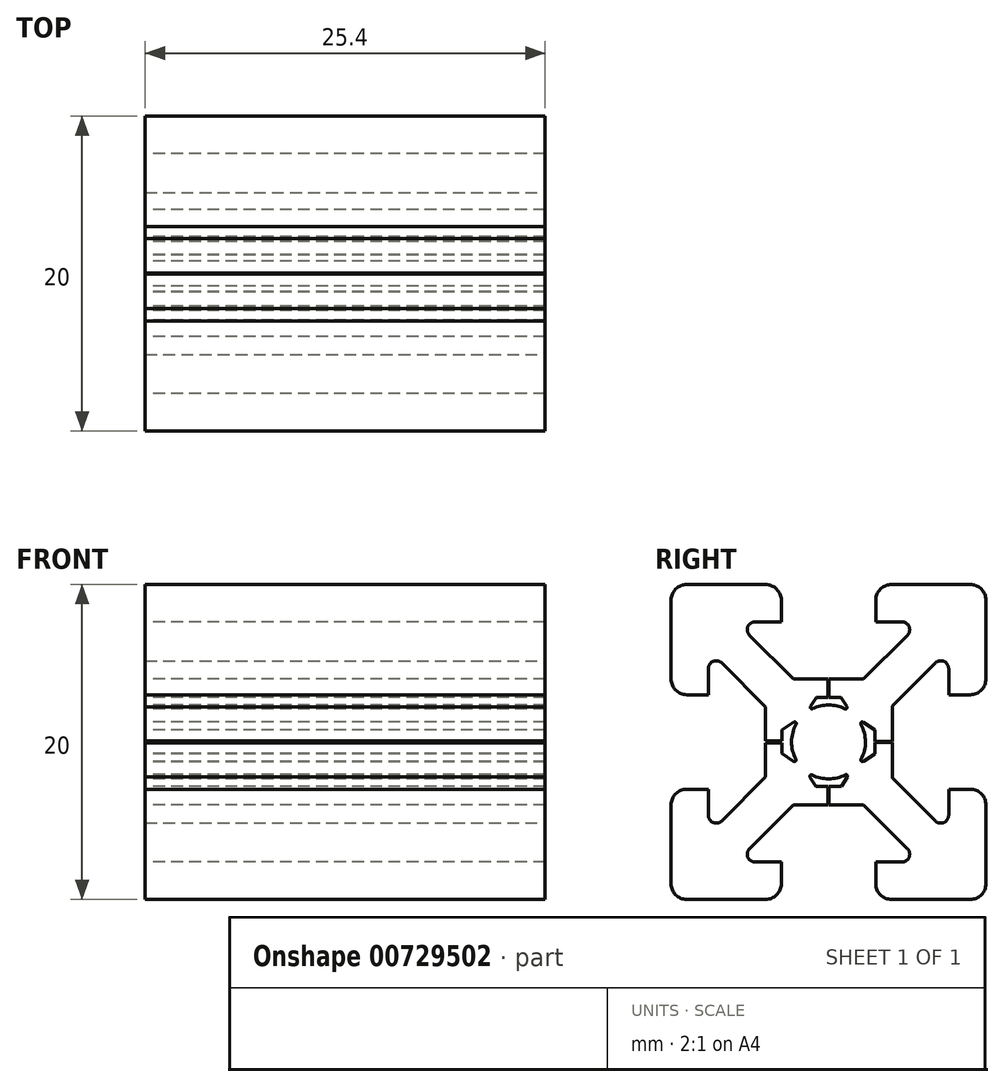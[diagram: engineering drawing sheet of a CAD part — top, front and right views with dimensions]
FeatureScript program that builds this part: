
annotation { "Feature Type Name" : "Feature", "Feature Type Description" : "" }
export const myFeature = defineFeature(function(context is Context, id is Id, definition is map)
    precondition{}
    {
        {
            var Q0;
            Q0=qCreatedBy(makeId("Top.planeOp"),FACE);
            var sketch = newSketch(context, id + "F0", { "sketchPlane" : qUnion([Q0])});
            skLineSegment(sketch, "E0", {"start": v(-15.81, 0) * mm, "end": v(2.4, 0) * mm, "construction": true});
            skLineSegment(sketch, "E1", {"start": v(0, 15.89) * mm, "end": v(0, -13.7) * mm, "construction": true});
            skLineSegment(sketch, "E2", {"start": v(0, 0) * mm, "end": v(-1.66, 1.66) * mm, "construction": true});
            skLineSegment(sketch, "E3", {"start": v(-2.3, 4.06) * mm, "end": v(-5.86, 7.63) * mm});
            skLineSegment(sketch, "E4", {"start": v(-5.86, 7.63) * mm, "end": v(-3, 7.63) * mm});
            skLineSegment(sketch, "E5", {"start": v(-3, 7.63) * mm, "end": v(-3, 10) * mm});
            skLineSegment(sketch, "E6", {"start": v(-3, 10) * mm, "end": v(-10, 10) * mm});
            skLineSegment(sketch, "E7.MirrorCS", {"start": v(-4, 2.23) * mm, "end": v(-7.63, 5.86) * mm});
            skLineSegment(sketch, "E8.MirrorCS", {"start": v(-7.63, 3) * mm, "end": v(-10, 3) * mm});
            skLineSegment(sketch, "E9.MirrorCS", {"start": v(-10, 3) * mm, "end": v(-10, 10) * mm});
            skLineSegment(sketch, "E10.MirrorCS", {"start": v(-7.63, 5.86) * mm, "end": v(-7.63, 3) * mm});
            skLineSegment(sketch, "E11.MirrorCS", {"start": v(3, 10) * mm, "end": v(10, 10) * mm});
            skLineSegment(sketch, "E12.MirrorCS", {"start": v(5.86, 7.63) * mm, "end": v(3, 7.63) * mm});
            skLineSegment(sketch, "E13.MirrorCS", {"start": v(3, 7.63) * mm, "end": v(3, 10) * mm});
            skLineSegment(sketch, "E14.MirrorCS", {"start": v(7.63, 5.86) * mm, "end": v(7.63, 3) * mm});
            skLineSegment(sketch, "E15.MirrorCS", {"start": v(10, 3) * mm, "end": v(10, 10) * mm});
            skLineSegment(sketch, "E16.MirrorCS", {"start": v(7.63, 3) * mm, "end": v(10, 3) * mm});
            skLineSegment(sketch, "E17.MirrorCS", {"start": v(2.3, 4.06) * mm, "end": v(5.86, 7.63) * mm});
            skLineSegment(sketch, "E18.MirrorCS", {"start": v(4, 2.23) * mm, "end": v(7.63, 5.86) * mm});
            skLineSegment(sketch, "E19.MirrorCS", {"start": v(5.86, -7.63) * mm, "end": v(3, -7.63) * mm});
            skLineSegment(sketch, "E20.MirrorCS", {"start": v(3, -10) * mm, "end": v(10, -10) * mm});
            skLineSegment(sketch, "E21.MirrorCS", {"start": v(-5.86, -7.63) * mm, "end": v(-3, -7.63) * mm});
            skLineSegment(sketch, "E22.MirrorCS", {"start": v(-3, -10) * mm, "end": v(-10, -10) * mm});
            skLineSegment(sketch, "E23.MirrorCS", {"start": v(-3, -7.63) * mm, "end": v(-3, -10) * mm});
            skLineSegment(sketch, "E24.MirrorCS", {"start": v(3, -7.63) * mm, "end": v(3, -10) * mm});
            skLineSegment(sketch, "E25.MirrorCS", {"start": v(7.63, -5.86) * mm, "end": v(7.63, -3) * mm});
            skLineSegment(sketch, "E26.MirrorCS", {"start": v(10, -3) * mm, "end": v(10, -10) * mm});
            skLineSegment(sketch, "E27.MirrorCS", {"start": v(4, -2.23) * mm, "end": v(7.63, -5.86) * mm});
            skLineSegment(sketch, "E28.MirrorCS", {"start": v(-7.63, -5.86) * mm, "end": v(-7.63, -3) * mm});
            skLineSegment(sketch, "E29.MirrorCS", {"start": v(-10, -3) * mm, "end": v(-10, -10) * mm});
            skLineSegment(sketch, "E30.MirrorCS", {"start": v(-7.63, -3) * mm, "end": v(-10, -3) * mm});
            skLineSegment(sketch, "E31.MirrorCS", {"start": v(-4, -2.23) * mm, "end": v(-7.63, -5.86) * mm});
            skLineSegment(sketch, "E32.MirrorCS", {"start": v(2.23, -4) * mm, "end": v(5.86, -7.63) * mm});
            skLineSegment(sketch, "E33.MirrorCS", {"start": v(-2.23, -4) * mm, "end": v(-5.86, -7.63) * mm});
            skLineSegment(sketch, "E34.MirrorCS", {"start": v(7.63, -3) * mm, "end": v(10, -3) * mm});
            skLineSegment(sketch, "E35", {"start": v(-4, 0) * mm, "end": v(-4, 0) * mm});
            skLineSegment(sketch, "E36", {"start": v(-2.3, 4.06) * mm, "end": v(-0.02, 4.06) * mm});
            skLineSegment(sketch, "E37.MirrorCS", {"start": v(-15.81, 8.12) * mm, "end": v(21.32, 8.12) * mm, "construction": true});
            skLineSegment(sketch, "E38", {"start": v(-4, 2.23) * mm, "end": v(-4, 0.02) * mm});
            skLineSegment(sketch, "E39", {"start": v(-2.23, -4) * mm, "end": v(-0.05, -4) * mm});
            skLineSegment(sketch, "E40", {"start": v(4, 2.23) * mm, "end": v(4, 0.03) * mm});
            skPoint(sketch, "E41.orphan", {"position": v(-0.59, 2.36) * mm});
            skPoint(sketch, "E42.orphan", {"position": v(-2.36, 0.59) * mm});
            skLineSegment(sketch, "E43.trimOffspring", {"start": v(0.03, 4.06) * mm, "end": v(2.3, 4.06) * mm});
            skPoint(sketch, "E44.orphan", {"position": v(0.59, 2.36) * mm});
            skPoint(sketch, "E45.orphan", {"position": v(2.36, 0.59) * mm});
            skPoint(sketch, "E46.orphan", {"position": v(-2.36, -0.59) * mm});
            skPoint(sketch, "E47.orphan", {"position": v(-0.59, -2.36) * mm});
            skPoint(sketch, "E48.orphan", {"position": v(0.59, -2.36) * mm});
            skPoint(sketch, "E49.orphan", {"position": v(2.36, -0.59) * mm});
            skLineSegment(sketch, "E50", {"start": v(-2.4, 0.03) * mm, "end": v(-2.4, 0.03) * mm});
            skLineSegment(sketch, "E51.MirrorCS", {"start": v(-2.4, -0.03) * mm, "end": v(-2.4, -0.03) * mm});
            skLineSegment(sketch, "E52.MirrorCS", {"start": v(2.4, 0.03) * mm, "end": v(2.4, 0.03) * mm});
            skLineSegment(sketch, "E53.MirrorCS", {"start": v(2.4, -0.03) * mm, "end": v(2.4, -0.03) * mm});
            skLineSegment(sketch, "E54.trimOffspring", {"start": v(4, -0.03) * mm, "end": v(4, -2.23) * mm});
            skLineSegment(sketch, "E55.trimOffspring", {"start": v(-4, -0.03) * mm, "end": v(-4, -2.23) * mm});
            skPoint(sketch, "E56.end.orphan", {"position": v(-2.4, 0) * mm});
            skPoint(sketch, "E57.orphan", {"position": v(-4, 0.03) * mm});
            skPoint(sketch, "E58.MirrorCS.end.orphan", {"position": v(2.4, 0) * mm});
            skPoint(sketch, "E58.MirrorCS.start.orphan", {"position": v(2.4, -0.03) * mm});
            skPoint(sketch, "E59.MirrorCS.start.orphan", {"position": v(2.4, 0.03) * mm});
            skLineSegment(sketch, "E60.trimOffspring", {"start": v(0.05, -4) * mm, "end": v(2.23, -4) * mm});
            skLineSegment(sketch, "E61", {"start": v(0, 0) * mm, "end": v(10, 10) * mm, "construction": true});
            skLineSegment(sketch, "E62", {"start": v(0, 0) * mm, "end": v(-10, -10) * mm, "construction": true});
            skLineSegment(sketch, "E63", {"start": v(10, -10) * mm, "end": v(0.07, 0.07) * mm, "construction": true});
            skPoint(sketch, "E64.start.orphan", {"position": v(-4, -0.03) * mm});
            skLineSegment(sketch, "E65", {"start": v(-2.82, -0.78) * mm, "end": v(-1.9, -1.37) * mm});
            skPoint(sketch, "E66.orphan", {"position": v(-1.66, -1.66) * mm});
            skPoint(sketch, "E67.orphan", {"position": v(0.03, -4.06) * mm});
            skPoint(sketch, "E68.orphan", {"position": v(-0.03, -4.06) * mm});
            skLineSegment(sketch, "E69", {"start": v(-2.82, 0.8) * mm, "end": v(-1.87, 1.41) * mm});
            skLineSegment(sketch, "E70", {"start": v(-0.76, 2.95) * mm, "end": v(-1.54, 1.77) * mm});
            skLineSegment(sketch, "E71", {"start": v(0.76, 2.95) * mm, "end": v(1.51, 1.8) * mm});
            skLineSegment(sketch, "E72", {"start": v(2.82, 0.8) * mm, "end": v(1.83, 1.46) * mm});
            skLineSegment(sketch, "E73", {"start": v(2.82, -0.8) * mm, "end": v(1.87, -1.41) * mm});
            skLineSegment(sketch, "E74.trimOffspring", {"start": v(1.8, -1.68) * mm, "end": v(1.82, -1.66) * mm});
            skLineSegment(sketch, "E75.trimOffspring", {"start": v(-8.12, 8.12) * mm, "end": v(-29.35, 29.35) * mm, "construction": true});
            skLineSegment(sketch, "E76", {"start": v(0.74, -2.96) * mm, "end": v(1.51, -1.8) * mm});
            skPoint(sketch, "E77.trimOffspring.start.orphan", {"position": v(0.33, -2.4) * mm});
            skPoint(sketch, "E78.MirrorCS.end.orphan", {"position": v(-0.33, -2.4) * mm});
            skLineSegment(sketch, "E79.trimOffspring", {"start": v(2.43, 0) * mm, "end": v(21.32, 0) * mm, "construction": true});
            skPoint(sketch, "E80.trimOffspring.start.orphan", {"position": v(0.33, 2.4) * mm});
            skPoint(sketch, "E81.trimOffspring.start.orphan", {"position": v(-0.33, 2.4) * mm});
            skArc(sketch, "E82", {"start": v(-1.87, 1.41) * mm, "mid": v(-2.35, 0.03) * mm, "end": v(-1.9, -1.37) * mm});
            skArc(sketch, "E83.trimOffspring", {"start": v(1.51, 1.8) * mm, "mid": v(-0.02, 2.35) * mm, "end": v(-1.54, 1.77) * mm});
            skArc(sketch, "E84.trimOffspring", {"start": v(1.87, -1.41) * mm, "mid": v(2.35, 0.03) * mm, "end": v(1.83, 1.46) * mm});
            skArc(sketch, "E85.trimOffspring", {"start": v(-1.55, -1.76) * mm, "mid": v(-0.03, -2.35) * mm, "end": v(1.51, -1.8) * mm});
            skLineSegment(sketch, "E86", {"start": v(-1.55, -1.76) * mm, "end": v(-0.75, -2.96) * mm});
            skLineSegment(sketch, "E87", {"start": v(-4, 0.03) * mm, "end": v(-2.82, 0.03) * mm});
            skLineSegment(sketch, "E88", {"start": v(-2.82, 0.03) * mm, "end": v(-2.82, 0.8) * mm});
            skLineSegment(sketch, "E89", {"start": v(-4, -0.03) * mm, "end": v(-2.82, -0.03) * mm});
            skLineSegment(sketch, "E90", {"start": v(-2.82, -0.03) * mm, "end": v(-2.82, -0.78) * mm});
            skLineSegment(sketch, "E91.MirrorCS", {"start": v(4, 0.03) * mm, "end": v(2.82, 0.03) * mm});
            skLineSegment(sketch, "E92.MirrorCS", {"start": v(4, -0.03) * mm, "end": v(2.82, -0.03) * mm});
            skLineSegment(sketch, "E93", {"start": v(2.82, 0.03) * mm, "end": v(2.82, 0.8) * mm});
            skLineSegment(sketch, "E94", {"start": v(2.82, -0.03) * mm, "end": v(2.82, -0.8) * mm});
            skLineSegment(sketch, "E95", {"start": v(-0.05, -4) * mm, "end": v(-0.05, -2.96) * mm});
            skLineSegment(sketch, "E96", {"start": v(-0.05, -2.96) * mm, "end": v(-0.75, -2.96) * mm});
            skLineSegment(sketch, "E97", {"start": v(0.05, -4) * mm, "end": v(0.05, -2.96) * mm});
            skLineSegment(sketch, "E98", {"start": v(0.05, -2.96) * mm, "end": v(0.74, -2.96) * mm});
            skLineSegment(sketch, "E99", {"start": v(-0.02, 4.06) * mm, "end": v(-0.02, 2.95) * mm});
            skLineSegment(sketch, "E100", {"start": v(-0.02, 2.95) * mm, "end": v(-0.76, 2.95) * mm});
            skLineSegment(sketch, "E101", {"start": v(0.03, 4.06) * mm, "end": v(0.03, 2.95) * mm});
            skLineSegment(sketch, "E102", {"start": v(0.03, 2.95) * mm, "end": v(0.76, 2.95) * mm});
            skSolve(sketch);
        }
        {
            var Q0;
            Q0=qSketchRegion(id+"F0",true);
            extrude(context, id + "F1", {"entities" : qUnion([Q0]), "depth" : 25.4 * mm, "offsetDistance" : 25.4 * mm});
        }
        {
            var Q0;
            Q0=makeQuery(id+"F1.opExtrude","SWEPT_EDGE",EDGE,{"disambiguationData":[OSD([sQuery(id+"F0.wireOp",EDGE,"E15.MirrorCS"),sQuery(id+"F0.wireOp",EDGE,"E11.MirrorCS")])]});
            var Q1;
            Q1=makeQuery(id+"F1.opExtrude","SWEPT_EDGE",EDGE,{"disambiguationData":[OSD([sQuery(id+"F0.wireOp",EDGE,"E20.MirrorCS"),sQuery(id+"F0.wireOp",EDGE,"E26.MirrorCS")])]});
            var Q2;
            Q2=makeQuery(id+"F1.opExtrude","SWEPT_EDGE",EDGE,{"disambiguationData":[OSD([sQuery(id+"F0.wireOp",EDGE,"E22.MirrorCS"),sQuery(id+"F0.wireOp",EDGE,"E29.MirrorCS")])]});
            var Q3;
            Q3=makeQuery(id+"F1.opExtrude","SWEPT_EDGE",EDGE,{"disambiguationData":[OSD([sQuery(id+"F0.wireOp",EDGE,"E22.MirrorCS"),sQuery(id+"F0.wireOp",EDGE,"E23.MirrorCS")])]});
            var Q4;
            Q4=makeQuery(id+"F1.opExtrude","SWEPT_EDGE",EDGE,{"disambiguationData":[OSD([sQuery(id+"F0.wireOp",EDGE,"E20.MirrorCS"),sQuery(id+"F0.wireOp",EDGE,"E24.MirrorCS")])]});
            var Q5;
            Q5=makeQuery(id+"F1.opExtrude","SWEPT_EDGE",EDGE,{"disambiguationData":[OSD([sQuery(id+"F0.wireOp",EDGE,"E5"),sQuery(id+"F0.wireOp",EDGE,"E6")])]});
            var Q6;
            Q6=makeQuery(id+"F1.opExtrude","SWEPT_EDGE",EDGE,{"disambiguationData":[OSD([sQuery(id+"F0.wireOp",EDGE,"E8.MirrorCS"),sQuery(id+"F0.wireOp",EDGE,"E9.MirrorCS")])]});
            var Q7;
            Q7=makeQuery(id+"F1.opExtrude","SWEPT_EDGE",EDGE,{"disambiguationData":[OSD([sQuery(id+"F0.wireOp",EDGE,"E15.MirrorCS"),sQuery(id+"F0.wireOp",EDGE,"E16.MirrorCS")])]});
            var Q8;
            Q8=makeQuery(id+"F1.opExtrude","SWEPT_EDGE",EDGE,{"disambiguationData":[OSD([sQuery(id+"F0.wireOp",EDGE,"E26.MirrorCS"),sQuery(id+"F0.wireOp",EDGE,"E34.MirrorCS")])]});
            var Q9;
            Q9=makeQuery(id+"F1.opExtrude","SWEPT_EDGE",EDGE,{"disambiguationData":[OSD([sQuery(id+"F0.wireOp",EDGE,"E29.MirrorCS"),sQuery(id+"F0.wireOp",EDGE,"E30.MirrorCS")])]});
            var Q10;
            Q10=makeQuery(id+"F1.opExtrude","SWEPT_EDGE",EDGE,{"disambiguationData":[OSD([sQuery(id+"F0.wireOp",EDGE,"E9.MirrorCS"),sQuery(id+"F0.wireOp",EDGE,"E6")])]});
            var Q11;
            Q11=makeQuery(id+"F1.opExtrude","SWEPT_EDGE",EDGE,{"disambiguationData":[OSD([sQuery(id+"F0.wireOp",EDGE,"E13.MirrorCS"),sQuery(id+"F0.wireOp",EDGE,"E11.MirrorCS")])]});
            fillet(context, id + "F2", {"entities" : qUnion([Q0, Q1, Q2, Q3, Q4, Q5, Q6, Q7, Q8, Q9, Q10, Q11]), "radius" : 1 * mm, "tangentPropagation" : true, "allowEdgeOverflow" : false});
        }
        {
            var Q0;
            Q0=makeQuery(id+"F1.opExtrude","SWEPT_EDGE",EDGE,{"disambiguationData":[OSD([sQuery(id+"F0.wireOp",EDGE,"E7.MirrorCS"),sQuery(id+"F0.wireOp",EDGE,"E10.MirrorCS")])]});
            var Q1;
            Q1=makeQuery(id+"F1.opExtrude","SWEPT_EDGE",EDGE,{"disambiguationData":[OSD([sQuery(id+"F0.wireOp",EDGE,"E3"),sQuery(id+"F0.wireOp",EDGE,"E4")])]});
            var Q2;
            Q2=makeQuery(id+"F1.opExtrude","SWEPT_EDGE",EDGE,{"disambiguationData":[OSD([sQuery(id+"F0.wireOp",EDGE,"E12.MirrorCS"),sQuery(id+"F0.wireOp",EDGE,"E17.MirrorCS")])]});
            var Q3;
            Q3=makeQuery(id+"F1.opExtrude","SWEPT_EDGE",EDGE,{"disambiguationData":[OSD([sQuery(id+"F0.wireOp",EDGE,"E14.MirrorCS"),sQuery(id+"F0.wireOp",EDGE,"E18.MirrorCS")])]});
            var Q4;
            Q4=makeQuery(id+"F1.opExtrude","SWEPT_EDGE",EDGE,{"disambiguationData":[OSD([sQuery(id+"F0.wireOp",EDGE,"E28.MirrorCS"),sQuery(id+"F0.wireOp",EDGE,"E31.MirrorCS")])]});
            var Q5;
            Q5=makeQuery(id+"F1.opExtrude","SWEPT_EDGE",EDGE,{"disambiguationData":[OSD([sQuery(id+"F0.wireOp",EDGE,"E21.MirrorCS"),sQuery(id+"F0.wireOp",EDGE,"E33.MirrorCS")])]});
            var Q6;
            Q6=makeQuery(id+"F1.opExtrude","SWEPT_EDGE",EDGE,{"disambiguationData":[OSD([sQuery(id+"F0.wireOp",EDGE,"E19.MirrorCS"),sQuery(id+"F0.wireOp",EDGE,"E32.MirrorCS")])]});
            var Q7;
            Q7=makeQuery(id+"F1.opExtrude","SWEPT_EDGE",EDGE,{"disambiguationData":[OSD([sQuery(id+"F0.wireOp",EDGE,"E25.MirrorCS"),sQuery(id+"F0.wireOp",EDGE,"E27.MirrorCS")])]});
            fillet(context, id + "F3", {"entities" : qUnion([Q0, Q1, Q2, Q3, Q4, Q5, Q6, Q7]), "radius" : .5 * mm, "tangentPropagation" : true, "allowEdgeOverflow" : false});
        }
        {
            var Q0;
            Q0=makeQuery(id+"F1.opExtrude","SWEPT_EDGE",EDGE,{"disambiguationData":[OSD([sQuery(id+"F0.wireOp",EDGE,"E69"),sQuery(id+"F0.wireOp",EDGE,"E82")])]});
            var Q1;
            Q1=makeQuery(id+"F1.opExtrude","SWEPT_EDGE",EDGE,{"disambiguationData":[OSD([sQuery(id+"F0.wireOp",EDGE,"E17.MirrorCS"),sQuery(id+"F0.wireOp",EDGE,"E43.trimOffspring")])]});
            var Q2;
            {var subQ0=sQuery(id+"F0.wireOp",EDGE,"E12.MirrorCS");Q2=makeQuery(id+"F3.opFillet","BLEND_EDGE",EDGE,{"blendedFrom":[makeQuery(id+"F1.opExtrude","SWEPT_EDGE",EDGE,{"disambiguationData":[OSD([subQ0,sQuery(id+"F0.wireOp",EDGE,"E17.MirrorCS")])]}),makeQuery(id+"F1.opExtrude","SWEPT_FACE",FACE,{"disambiguationData":[OSD([subQ0])]})],"blendedInto":[makeQuery(id+"F1.opExtrude","SWEPT_FACE",FACE,{"disambiguationData":[OSD([subQ0])]})]});}
            var Q3;
            Q3=makeQuery(id+"F1.opExtrude","SWEPT_EDGE",EDGE,{"disambiguationData":[OSD([sQuery(id+"F0.wireOp",EDGE,"E70"),sQuery(id+"F0.wireOp",EDGE,"E83.trimOffspring")])]});
            var Q4;
            Q4=makeQuery(id+"F1.opExtrude","SWEPT_EDGE",EDGE,{"disambiguationData":[OSD([sQuery(id+"F0.wireOp",EDGE,"VnvyymTW-JKNP-Vp1J-SOXt-zXPDHYCny5Fm"),sQuery(id+"F0.wireOp",EDGE,"E85.trimOffspring")])]});
            var Q5;
            Q5=makeQuery(id+"F1.opExtrude","SWEPT_EDGE",EDGE,{"disambiguationData":[OSD([sQuery(id+"F0.wireOp",EDGE,"E76"),sQuery(id+"F0.wireOp",EDGE,"E85.trimOffspring")])]});
            var Q6;
            Q6=makeQuery(id+"F1.opExtrude","SWEPT_EDGE",EDGE,{"disambiguationData":[OSD([sQuery(id+"F0.wireOp",EDGE,"E73"),sQuery(id+"F0.wireOp",EDGE,"E84.trimOffspring")])]});
            var Q7;
            Q7=makeQuery(id+"F1.opExtrude","SWEPT_EDGE",EDGE,{"disambiguationData":[OSD([sQuery(id+"F0.wireOp",EDGE,"E72"),sQuery(id+"F0.wireOp",EDGE,"E84.trimOffspring")])]});
            var Q8;
            Q8=makeQuery(id+"F1.opExtrude","SWEPT_EDGE",EDGE,{"disambiguationData":[OSD([sQuery(id+"F0.wireOp",EDGE,"E71"),sQuery(id+"F0.wireOp",EDGE,"E83.trimOffspring")])]});
            var Q9;
            Q9=makeQuery(id+"F1.opExtrude","SWEPT_EDGE",EDGE,{"disambiguationData":[OSD([sQuery(id+"F0.wireOp",EDGE,"E65"),sQuery(id+"F0.wireOp",EDGE,"E82")])]});
            fillet(context, id + "F4", {"entities" : qUnion([Q0, Q1, Q2, Q3, Q4, Q5, Q6, Q7, Q8, Q9]), "radius" : .1 * mm, "tangentPropagation" : true, "allowEdgeOverflow" : false});
        }
        {
            var Q0;
            Q0=makeQuery(id+"F1.opExtrude","SWEPT_BODY",BODY,{"disambiguationData":[OSD([sQuery(id+"F0.wireOp",EDGE,"E3"),sQuery(id+"F0.wireOp",EDGE,"E7.MirrorCS"),sQuery(id+"F0.wireOp",EDGE,"E8.MirrorCS"),sQuery(id+"F0.wireOp",EDGE,"E9.MirrorCS"),sQuery(id+"F0.wireOp",EDGE,"E10.MirrorCS"),sQuery(id+"F0.wireOp",EDGE,"E5"),sQuery(id+"F0.wireOp",EDGE,"E6"),sQuery(id+"F0.wireOp",EDGE,"E4"),sQuery(id+"F0.wireOp",EDGE,"E14.MirrorCS"),sQuery(id+"F0.wireOp",EDGE,"E15.MirrorCS"),sQuery(id+"F0.wireOp",EDGE,"E16.MirrorCS"),sQuery(id+"F0.wireOp",EDGE,"E12.MirrorCS"),sQuery(id+"F0.wireOp",EDGE,"E17.MirrorCS"),sQuery(id+"F0.wireOp",EDGE,"E18.MirrorCS"),sQuery(id+"F0.wireOp",EDGE,"E13.MirrorCS"),sQuery(id+"F0.wireOp",EDGE,"E11.MirrorCS"),sQuery(id+"F0.wireOp",EDGE,"E21.MirrorCS"),sQuery(id+"F0.wireOp",EDGE,"E19.MirrorCS"),sQuery(id+"F0.wireOp",EDGE,"E20.MirrorCS"),sQuery(id+"F0.wireOp",EDGE,"E24.MirrorCS"),sQuery(id+"F0.wireOp",EDGE,"E25.MirrorCS"),sQuery(id+"F0.wireOp",EDGE,"E26.MirrorCS"),sQuery(id+"F0.wireOp",EDGE,"E27.MirrorCS"),sQuery(id+"F0.wireOp",EDGE,"E22.MirrorCS"),sQuery(id+"F0.wireOp",EDGE,"E28.MirrorCS"),sQuery(id+"F0.wireOp",EDGE,"E29.MirrorCS"),sQuery(id+"F0.wireOp",EDGE,"E30.MirrorCS"),sQuery(id+"F0.wireOp",EDGE,"E31.MirrorCS"),sQuery(id+"F0.wireOp",EDGE,"E23.MirrorCS"),sQuery(id+"F0.wireOp",EDGE,"E32.MirrorCS"),sQuery(id+"F0.wireOp",EDGE,"E33.MirrorCS"),sQuery(id+"F0.wireOp",EDGE,"E34.MirrorCS"),sQuery(id+"F0.wireOp",EDGE,"E36"),sQuery(id+"F0.wireOp",EDGE,"E38"),sQuery(id+"F0.wireOp",EDGE,"E39"),sQuery(id+"F0.wireOp",EDGE,"E40"),sQuery(id+"F0.wireOp",EDGE,"E43.trimOffspring"),sQuery(id+"F0.wireOp",EDGE,"E54.trimOffspring"),sQuery(id+"F0.wireOp",EDGE,"E55.trimOffspring"),sQuery(id+"F0.wireOp",EDGE,"E60.trimOffspring"),sQuery(id+"F0.wireOp",EDGE,"E65"),sQuery(id+"F0.wireOp",EDGE,"E69"),sQuery(id+"F0.wireOp",EDGE,"E70"),sQuery(id+"F0.wireOp",EDGE,"E71"),sQuery(id+"F0.wireOp",EDGE,"E72"),sQuery(id+"F0.wireOp",EDGE,"E73"),sQuery(id+"F0.wireOp",EDGE,"E76"),sQuery(id+"F0.wireOp",EDGE,"E82"),sQuery(id+"F0.wireOp",EDGE,"E83.trimOffspring"),sQuery(id+"F0.wireOp",EDGE,"E84.trimOffspring"),sQuery(id+"F0.wireOp",EDGE,"E85.trimOffspring"),sQuery(id+"F0.wireOp",EDGE,"E86"),sQuery(id+"F0.wireOp",EDGE,"E87"),sQuery(id+"F0.wireOp",EDGE,"E88"),sQuery(id+"F0.wireOp",EDGE,"E89"),sQuery(id+"F0.wireOp",EDGE,"E90"),sQuery(id+"F0.wireOp",EDGE,"E91.MirrorCS"),sQuery(id+"F0.wireOp",EDGE,"E92.MirrorCS"),sQuery(id+"F0.wireOp",EDGE,"E93"),sQuery(id+"F0.wireOp",EDGE,"E94"),sQuery(id+"F0.wireOp",EDGE,"E95"),sQuery(id+"F0.wireOp",EDGE,"E96"),sQuery(id+"F0.wireOp",EDGE,"E97"),sQuery(id+"F0.wireOp",EDGE,"E98"),sQuery(id+"F0.wireOp",EDGE,"E99"),sQuery(id+"F0.wireOp",EDGE,"E100"),sQuery(id+"F0.wireOp",EDGE,"E101"),sQuery(id+"F0.wireOp",EDGE,"E102")])]});
            var Q1;
            Q1=makeQuery(id+"F1.opExtrude","CAP_EDGE",EDGE,{"disambiguationData":[OSD([sQuery(id+"F0.wireOp",EDGE,"E15.MirrorCS")])],"isStart":false});
            transform(context, id + "F5", {"entities" : qUnion([Q0]), "transformType" : TransformType.ROTATION, "transformAxis" : qUnion([Q1]), "angle" : 90 * degree, "makeCopy" : false});
        }
        {
            var Q0;
            Q0=makeQuery(id+"F1.opExtrude","SWEPT_BODY",BODY,{"disambiguationData":[OSD([sQuery(id+"F0.wireOp",EDGE,"E3"),sQuery(id+"F0.wireOp",EDGE,"E7.MirrorCS"),sQuery(id+"F0.wireOp",EDGE,"E8.MirrorCS"),sQuery(id+"F0.wireOp",EDGE,"E9.MirrorCS"),sQuery(id+"F0.wireOp",EDGE,"E10.MirrorCS"),sQuery(id+"F0.wireOp",EDGE,"E5"),sQuery(id+"F0.wireOp",EDGE,"E6"),sQuery(id+"F0.wireOp",EDGE,"E4"),sQuery(id+"F0.wireOp",EDGE,"E14.MirrorCS"),sQuery(id+"F0.wireOp",EDGE,"E15.MirrorCS"),sQuery(id+"F0.wireOp",EDGE,"E16.MirrorCS"),sQuery(id+"F0.wireOp",EDGE,"E12.MirrorCS"),sQuery(id+"F0.wireOp",EDGE,"E17.MirrorCS"),sQuery(id+"F0.wireOp",EDGE,"E18.MirrorCS"),sQuery(id+"F0.wireOp",EDGE,"E13.MirrorCS"),sQuery(id+"F0.wireOp",EDGE,"E11.MirrorCS"),sQuery(id+"F0.wireOp",EDGE,"E21.MirrorCS"),sQuery(id+"F0.wireOp",EDGE,"E19.MirrorCS"),sQuery(id+"F0.wireOp",EDGE,"E20.MirrorCS"),sQuery(id+"F0.wireOp",EDGE,"E24.MirrorCS"),sQuery(id+"F0.wireOp",EDGE,"E25.MirrorCS"),sQuery(id+"F0.wireOp",EDGE,"E26.MirrorCS"),sQuery(id+"F0.wireOp",EDGE,"E27.MirrorCS"),sQuery(id+"F0.wireOp",EDGE,"E22.MirrorCS"),sQuery(id+"F0.wireOp",EDGE,"E28.MirrorCS"),sQuery(id+"F0.wireOp",EDGE,"E29.MirrorCS"),sQuery(id+"F0.wireOp",EDGE,"E30.MirrorCS"),sQuery(id+"F0.wireOp",EDGE,"E31.MirrorCS"),sQuery(id+"F0.wireOp",EDGE,"E23.MirrorCS"),sQuery(id+"F0.wireOp",EDGE,"E32.MirrorCS"),sQuery(id+"F0.wireOp",EDGE,"E33.MirrorCS"),sQuery(id+"F0.wireOp",EDGE,"E34.MirrorCS"),sQuery(id+"F0.wireOp",EDGE,"E36"),sQuery(id+"F0.wireOp",EDGE,"E38"),sQuery(id+"F0.wireOp",EDGE,"E39"),sQuery(id+"F0.wireOp",EDGE,"E40"),sQuery(id+"F0.wireOp",EDGE,"E43.trimOffspring"),sQuery(id+"F0.wireOp",EDGE,"E54.trimOffspring"),sQuery(id+"F0.wireOp",EDGE,"E55.trimOffspring"),sQuery(id+"F0.wireOp",EDGE,"E60.trimOffspring"),sQuery(id+"F0.wireOp",EDGE,"E65"),sQuery(id+"F0.wireOp",EDGE,"E69"),sQuery(id+"F0.wireOp",EDGE,"E70"),sQuery(id+"F0.wireOp",EDGE,"E71"),sQuery(id+"F0.wireOp",EDGE,"E72"),sQuery(id+"F0.wireOp",EDGE,"E73"),sQuery(id+"F0.wireOp",EDGE,"E76"),sQuery(id+"F0.wireOp",EDGE,"E82"),sQuery(id+"F0.wireOp",EDGE,"E83.trimOffspring"),sQuery(id+"F0.wireOp",EDGE,"E84.trimOffspring"),sQuery(id+"F0.wireOp",EDGE,"E85.trimOffspring"),sQuery(id+"F0.wireOp",EDGE,"E86"),sQuery(id+"F0.wireOp",EDGE,"E87"),sQuery(id+"F0.wireOp",EDGE,"E88"),sQuery(id+"F0.wireOp",EDGE,"E89"),sQuery(id+"F0.wireOp",EDGE,"E90"),sQuery(id+"F0.wireOp",EDGE,"E91.MirrorCS"),sQuery(id+"F0.wireOp",EDGE,"E92.MirrorCS"),sQuery(id+"F0.wireOp",EDGE,"E93"),sQuery(id+"F0.wireOp",EDGE,"E94"),sQuery(id+"F0.wireOp",EDGE,"E95"),sQuery(id+"F0.wireOp",EDGE,"E96"),sQuery(id+"F0.wireOp",EDGE,"E97"),sQuery(id+"F0.wireOp",EDGE,"E98"),sQuery(id+"F0.wireOp",EDGE,"E99"),sQuery(id+"F0.wireOp",EDGE,"E100"),sQuery(id+"F0.wireOp",EDGE,"E101"),sQuery(id+"F0.wireOp",EDGE,"E102")])]});
            transform(context, id + "F6", {"entities" : qUnion([Q0]), "transformType" : TransformType.TRANSLATION_3D, "dx" : 0 * mm, "dy" : 0 * mm, "dz" : -350.52 * mm, "makeCopy" : false});
        }
    });
